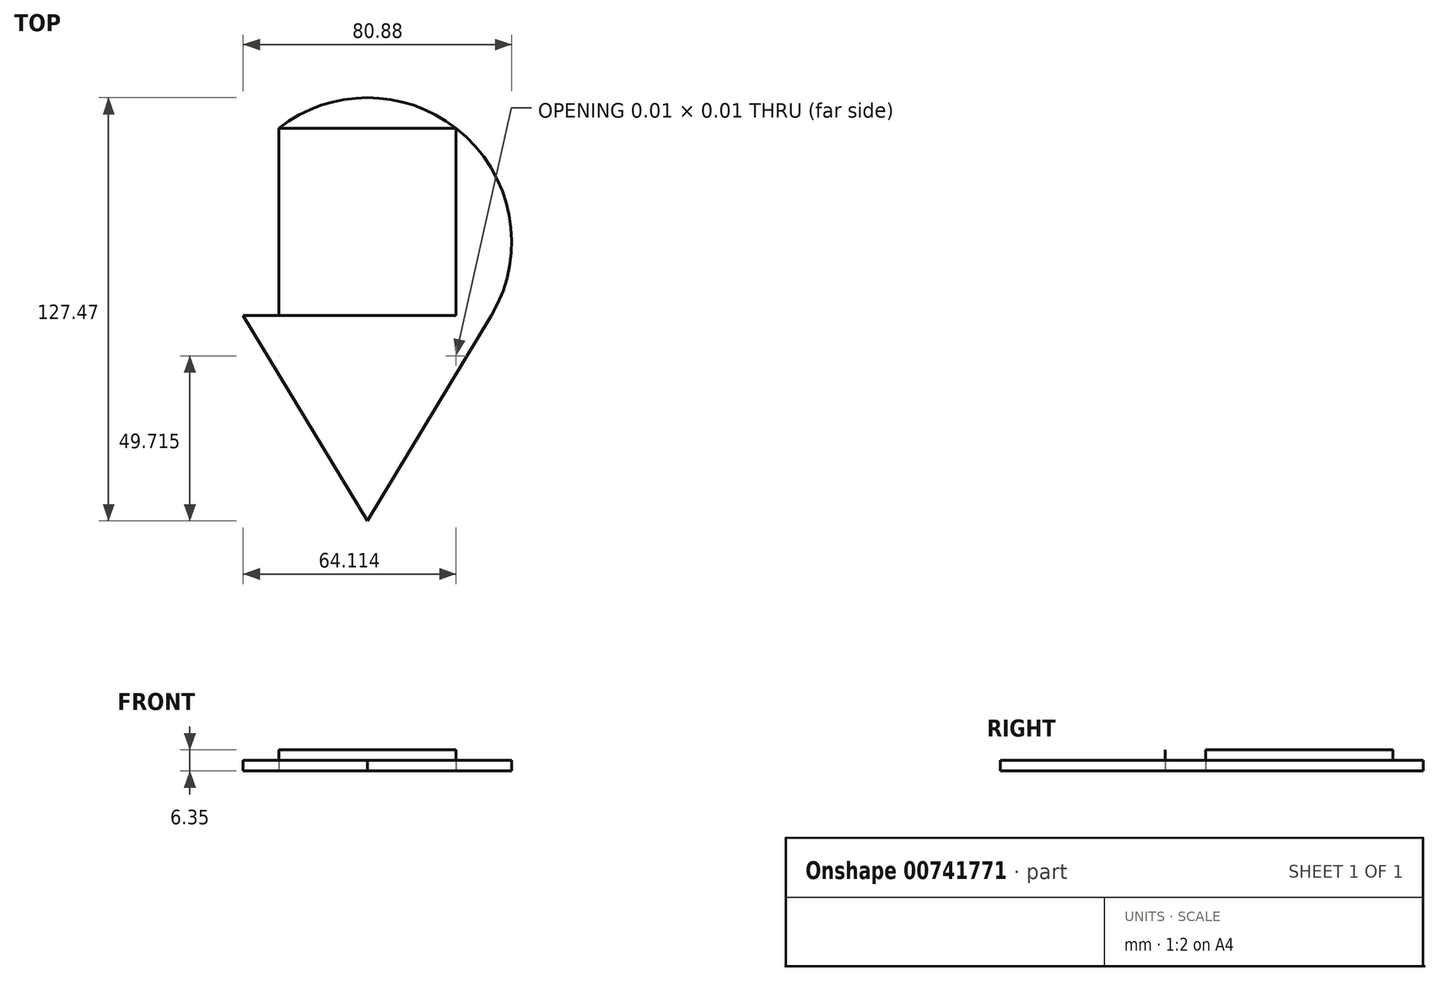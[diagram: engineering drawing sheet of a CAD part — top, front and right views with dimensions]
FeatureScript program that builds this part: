
annotation { "Feature Type Name" : "Feature", "Feature Type Description" : "" }
export const myFeature = defineFeature(function(context is Context, id is Id, definition is map)
    precondition{}
    {
        {
            var Q0;
            Q0=qCreatedBy(makeId("Top.planeOp"),FACE);
            var sketch = newSketch(context, id + "F0", { "sketchPlane" : qUnion([Q0])});
            skLineSegment(sketch, "E0.bottom", {"start": v(-53.4, 68.6) * mm, "end": v(0, 68.6) * mm});
            skLineSegment(sketch, "E0.top", {"start": v(-53.4, 0) * mm, "end": v(-53.39, 0) * mm});
            skLineSegment(sketch, "E0.left", {"start": v(-53.4, 68.6) * mm, "end": v(-53.4, 0) * mm});
            skLineSegment(sketch, "E0.right", {"start": v(0, 68.6) * mm, "end": v(0, 0) * mm});
            skLineSegment(sketch, "E1", {"start": v(-26.7, 68.6) * mm, "end": v(-26.7, -49.71) * mm, "construction": true});
            skPoint(sketch, "E2", {"position": v(-26.7, 34.3) * mm});
            skLineSegment(sketch, "E3", {"start": v(-26.7, 34.3) * mm, "end": v(-53.4, 0) * mm, "construction": true});
            skArc(sketch, "E4", {"start": v(-53.4, 0) * mm, "mid": v(-53.4, 0) * mm, "end": v(-53.39, 0) * mm});
            skPoint(sketch, "E5.orphan", {"position": v(-26.7, 0) * mm});
            skLineSegment(sketch, "E6", {"start": v(10.72, 12.2) * mm, "end": v(-26.7, -49.71) * mm});
            skLineSegment(sketch, "E7", {"start": v(10.72, 12.2) * mm, "end": v(-64.12, 12.2) * mm});
            skLineSegment(sketch, "E8", {"start": v(-64.12, 12.2) * mm, "end": v(-26.7, -49.71) * mm});
            skArc(sketch, "E9.trimOffspring", {"start": v(-0.01, 0) * mm, "mid": v(0, 0) * mm, "end": v(0, 0) * mm});
            skArc(sketch, "E10.trimOffspring", {"start": v(10.27, 11.45) * mm, "mid": v(-26.7, 77.76) * mm, "end": v(-63.67, 11.45) * mm});
            skLineSegment(sketch, "E11.0", {"start": v(13.43, 10.55) * mm, "end": v(-26.7, -55.85) * mm});
            skLineSegment(sketch, "E11.1", {"start": v(-66.83, 10.55) * mm, "end": v(-26.7, -55.85) * mm});
            skLineSegment(sketch, "E12", {"start": v(-63.67, 11.45) * mm, "end": v(-66.83, 10.55) * mm});
            skLineSegment(sketch, "E13", {"start": v(13.43, 10.55) * mm, "end": v(10.72, 12.2) * mm});
            skArc(sketch, "E14", {"start": v(1.74, -2.66) * mm, "mid": v(-26.7, 80.93) * mm, "end": v(-55.14, -2.66) * mm});
            skLineSegment(sketch, "E15.trimOffspring", {"start": v(-26.7, 0) * mm, "end": v(0, 0) * mm});
            skLineSegment(sketch, "E16.0", {"start": v(3.18, 68.6) * mm, "end": v(3.18, 0) * mm});
            skSolve(sketch);
        }
        {
            var Q0;
            {var subQ0=sQuery(id+"F0.wireOp",EDGE,"E4");var subQ1=sQuery(id+"F0.wireOp",EDGE,"E0.left");var subQ2=makeQuery(id+"F0.imprint","INTERSECT",VERTEX,{"disambiguationData":[OD(0.0)],"derivedFrom":[subQ1,subQ0]});Q0=makeQuery(id+"F0.imprint","IMPRINT",FACE,{"disambiguationData":[TD([[makeQuery(id+"F0.imprint","IMPRINT",EDGE,{"disambiguationData":[TD([[subQ2,-1.0]])],"derivedFrom":subQ1}),-1.0]])]});}
            var Q1;
            {var subQ0=sQuery(id+"F0.wireOp",EDGE,"E4");var subQ1=sQuery(id+"F0.wireOp",EDGE,"E0.top");var subQ2=makeQuery(id+"F0.imprint","INTERSECT",VERTEX,{"disambiguationData":[OD(0.0)],"derivedFrom":[subQ1,subQ0]});Q1=makeQuery(id+"F0.imprint","IMPRINT",FACE,{"disambiguationData":[TD([[makeQuery(id+"F0.imprint","IMPRINT",EDGE,{"disambiguationData":[TD([[subQ2,-1.0]])],"derivedFrom":subQ1}),-1.0]])]});}
            var Q2;
            {var subQ6=sQuery(id+"F0.wireOp",EDGE,"2fhuC0no-GH0m-5FQ5-pQYY-wwpoj4rK3rvi");Q2=makeQuery(id+"F0.imprint","IMPRINT",FACE,{"disambiguationData":[TD([[makeQuery(id+"F0.imprint","IMPRINT",EDGE,{"derivedFrom":subQ6}),1.0]])]});}
            var Q3;
            {var subQ0=sQuery(id+"F0.wireOp",EDGE,"E4");var subQ1=sQuery(id+"F0.wireOp",EDGE,"E0.right");var subQ2=makeQuery(id+"F0.imprint","INTERSECT",VERTEX,{"disambiguationData":[OD(0.0)],"derivedFrom":[subQ1,subQ0]});Q3=makeQuery(id+"F0.imprint","IMPRINT",FACE,{"disambiguationData":[TD([[makeQuery(id+"F0.imprint","IMPRINT",EDGE,{"disambiguationData":[TD([[subQ2,-1.0]])],"derivedFrom":subQ1}),1.0]])]});}
            var Q4;
            {var subQ0=sQuery(id+"F0.wireOp",EDGE,"E4");var subQ1=sQuery(id+"F0.wireOp",EDGE,"E0.bottom");var subQ2=makeQuery(id+"F0.imprint","INTERSECT",VERTEX,{"disambiguationData":[OD(0.0)],"derivedFrom":[subQ1,subQ0]});Q4=makeQuery(id+"F0.imprint","IMPRINT",FACE,{"disambiguationData":[TD([[makeQuery(id+"F0.imprint","IMPRINT",EDGE,{"disambiguationData":[TD([[subQ2,-1.0]])],"derivedFrom":subQ1}),1.0]])]});}
            var Q5;
            {var subQ0=sQuery(id+"F0.wireOp",EDGE,"E7");var subQ1=sQuery(id+"F0.wireOp",EDGE,"E0.left");var subQ2=makeQuery(id+"F0.imprint","INTERSECT",VERTEX,{"derivedFrom":[subQ1,subQ0]});Q5=makeQuery(id+"F0.imprint","IMPRINT",FACE,{"disambiguationData":[TD([[makeQuery(id+"F0.imprint","IMPRINT",EDGE,{"disambiguationData":[TD([[subQ2,-1.0]])],"derivedFrom":subQ1}),-1.0]])]});}
            var Q6;
            {var subQ0=sQuery(id+"F0.wireOp",EDGE,"E0.left");var subQ1=sQuery(id+"F0.wireOp",EDGE,"E0.top");var subQ2=makeQuery(id+"F0.imprint","INTERSECT",VERTEX,{"derivedFrom":[subQ1,subQ0]});Q6=makeQuery(id+"F0.imprint","IMPRINT",FACE,{"disambiguationData":[TD([[makeQuery(id+"F0.imprint","IMPRINT",EDGE,{"disambiguationData":[TD([[subQ2,-1.0]])],"derivedFrom":subQ1}),-1.0]])]});}
            var Q7;
            {var subQ0=sQuery(id+"F0.wireOp",EDGE,"E7");var subQ1=sQuery(id+"F0.wireOp",EDGE,"E0.right");var subQ2=makeQuery(id+"F0.imprint","INTERSECT",VERTEX,{"derivedFrom":[subQ1,subQ0]});Q7=makeQuery(id+"F0.imprint","IMPRINT",FACE,{"disambiguationData":[TD([[makeQuery(id+"F0.imprint","IMPRINT",EDGE,{"disambiguationData":[TD([[subQ2,-1.0]])],"derivedFrom":subQ1}),1.0]])]});}
            var Q8;
            {var subQ1=sQuery(id+"F0.wireOp",EDGE,"E7");var subQ3=sQuery(id+"F0.wireOp",EDGE,"113c3180-6c96-49cc-aea7-bd01cf957f55.0");var subQ4=makeQuery(id+"F0.imprint","INTERSECT",VERTEX,{"derivedFrom":[subQ1,subQ3]});Q8=makeQuery(id+"F0.imprint","IMPRINT",FACE,{"disambiguationData":[TD([[makeQuery(id+"F0.imprint","IMPRINT",EDGE,{"disambiguationData":[TD([[subQ4,1.0]])],"derivedFrom":subQ3}),-1.0]])]});}
            var Q9;
            {var subQ0=sQuery(id+"F0.wireOp",EDGE,"E10.trimOffspring");var subQ1=sQuery(id+"F0.wireOp",EDGE,"E0.bottom");var subQ2=makeQuery(id+"F0.imprint","INTERSECT",VERTEX,{"disambiguationData":[OD(0.0)],"derivedFrom":[subQ1,subQ0]});Q9=makeQuery(id+"F0.imprint","IMPRINT",FACE,{"disambiguationData":[TD([[makeQuery(id+"F0.imprint","IMPRINT",EDGE,{"disambiguationData":[TD([[subQ2,-1.0]])],"derivedFrom":subQ1}),1.0]])]});}
            var Q10;
            {var subQ1=sQuery(id+"F0.wireOp",EDGE,"E7");var subQ3=sQuery(id+"F0.wireOp",EDGE,"E16.0");var subQ4=makeQuery(id+"F0.imprint","INTERSECT",VERTEX,{"derivedFrom":[subQ1,subQ3]});Q10=makeQuery(id+"F0.imprint","IMPRINT",FACE,{"disambiguationData":[TD([[makeQuery(id+"F0.imprint","IMPRINT",EDGE,{"disambiguationData":[TD([[subQ4,1.0]])],"derivedFrom":subQ3}),1.0]])]});}
            extrude(context, id + "F1", {"entities" : qUnion([Q0, Q1, Q2, Q3, Q4, Q5, Q6, Q7, Q8, Q9, Q10]), "depth" : 3.17 * mm, "offsetDistance" : 25.4 * mm});
        }
        {
            var Q0;
            {var subQ0=sQuery(id+"F0.wireOp",EDGE,"E4");var subQ10=sQuery(id+"F0.wireOp",EDGE,"E0.bottom");var subQ11=makeQuery(id+"F0.imprint","INTERSECT",VERTEX,{"disambiguationData":[OD(0.0)],"derivedFrom":[subQ10,subQ0]});Q0=makeQuery(id+"F0.imprint","IMPRINT",FACE,{"disambiguationData":[TD([[makeQuery(id+"F0.imprint","IMPRINT",EDGE,{"disambiguationData":[TD([[subQ11,-1.0]])],"derivedFrom":subQ10}),-1.0]])]});}
            var Q1;
            {var subQ0=sQuery(id+"F0.wireOp",EDGE,"E4");var subQ1=sQuery(id+"F0.wireOp",EDGE,"E0.top");var subQ2=makeQuery(id+"F0.imprint","INTERSECT",VERTEX,{"disambiguationData":[OD(0.0)],"derivedFrom":[subQ1,subQ0]});Q1=makeQuery(id+"F0.imprint","IMPRINT",FACE,{"disambiguationData":[TD([[makeQuery(id+"F0.imprint","IMPRINT",EDGE,{"disambiguationData":[TD([[subQ2,-1.0]])],"derivedFrom":subQ1}),1.0]])]});}
            extrude(context, id + "F2", {"entities" : qUnion([Q0, Q1]), "operationType" : NewBodyOperationType.ADD, "depth" : 6.35 * mm, "offsetDistance" : 25.4 * mm});
        }
    });
